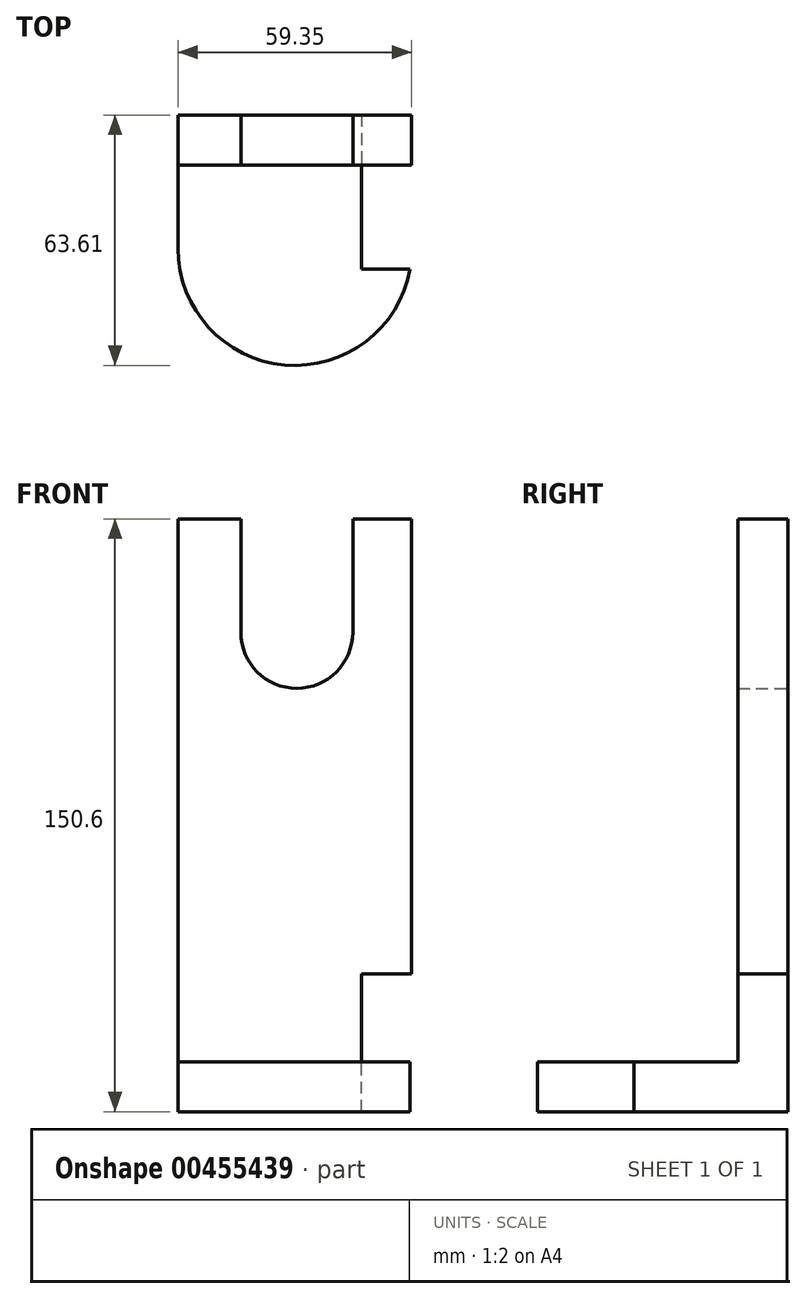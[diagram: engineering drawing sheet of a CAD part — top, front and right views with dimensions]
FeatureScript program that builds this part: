
annotation { "Feature Type Name" : "Feature", "Feature Type Description" : "" }
export const myFeature = defineFeature(function(context is Context, id is Id, definition is map)
    precondition{}
    {
        {
            var Q0;
            Q0=qCreatedBy(makeId("Front.planeOp"),FACE);
            var sketch = newSketch(context, id + "F0", { "sketchPlane" : qUnion([Q0])});
            skLineSegment(sketch, "E0", {"start": v(-52.9, 53.85) * mm, "end": v(-36.97, 53.85) * mm});
            skLineSegment(sketch, "E1", {"start": v(-36.97, 53.85) * mm, "end": v(-36.97, 25.03) * mm});
            skLineSegment(sketch, "E2", {"start": v(-52.9, 53.85) * mm, "end": v(-52.9, -84.05) * mm});
            skLineSegment(sketch, "E3", {"start": v(-52.9, -84.05) * mm, "end": v(6.45, -84.05) * mm});
            skLineSegment(sketch, "E4", {"start": v(6.45, -84.05) * mm, "end": v(6.45, 53.85) * mm});
            skLineSegment(sketch, "E5", {"start": v(6.45, 53.85) * mm, "end": v(-8.53, 53.85) * mm});
            skLineSegment(sketch, "E6", {"start": v(-8.53, 53.85) * mm, "end": v(-8.53, 25.03) * mm});
            skArc(sketch, "E7", {"start": v(-36.97, 25.03) * mm, "mid": v(-22.75, 10.8) * mm, "end": v(-8.53, 25.03) * mm});
            skSolve(sketch);
        }
        {
            var Q0;
            Q0 = qSketchRegion(id + "F0", true);
            extrude(context, id + "F1", {"entities" : qUnion([Q0]), "depth" : 12.7 * mm});
        }
        {
            var Q0;
            Q0=makeQuery(id+"F1.opExtrude","SWEPT_FACE",FACE,{"disambiguationData":[OSD([sQuery(id+"F0.wireOp",EDGE,"E3")])]});
            var sketch = newSketch(context, id + "F2", { "sketchPlane" : qUnion([Q0])});
            skLineSegment(sketch, "E8.bottom", {"start": v(6.45, 0) * mm, "end": v(-52.9, 0) * mm});
            skLineSegment(sketch, "E8.top", {"start": v(6.45, 33.94) * mm, "end": v(-52.9, 33.94) * mm});
            skLineSegment(sketch, "E8.left", {"start": v(6.45, 0) * mm, "end": v(6.45, 33.94) * mm});
            skLineSegment(sketch, "E8.right", {"start": v(-52.9, 0) * mm, "end": v(-52.9, 33.94) * mm});
            skArc(sketch, "E9", {"start": v(-52.9, 33.94) * mm, "mid": v(-23.23, 63.6) * mm, "end": v(6.45, 33.94) * mm});
            skSolve(sketch);
        }
        {
            var Q0;
            Q0 = qSketchRegion(id + "F2", true);
            extrude(context, id + "F3", {"entities" : qUnion([Q0]), "operationType" : NewBodyOperationType.ADD, "depth" : 12.7 * mm});
        }
        {
            var Q0;
            Q0=makeQuery(id+"F3.boolean.opBoolean","MERGE",FACE,{"derivedFrom":[makeQuery(id+"F1.opExtrude","SWEPT_FACE",FACE,{"disambiguationData":[OSD([sQuery(id+"F0.wireOp",EDGE,"E4")])]}),makeQuery(id+"F3.opExtrude","SWEPT_FACE",FACE,{"disambiguationData":[OSD([sQuery(id+"F2.wireOp",EDGE,"E8.left")])]})]});
            var sketch = newSketch(context, id + "F4", { "sketchPlane" : qUnion([Q0])});
            skLineSegment(sketch, "E10.bottom", {"start": v(0, -96.75) * mm, "end": v(-39.16, -96.75) * mm});
            skLineSegment(sketch, "E10.top", {"start": v(0, -61.7) * mm, "end": v(-39.16, -61.7) * mm});
            skLineSegment(sketch, "E10.left", {"start": v(0, -96.75) * mm, "end": v(0, -61.7) * mm});
            skLineSegment(sketch, "E10.right", {"start": v(-39.16, -96.75) * mm, "end": v(-39.16, -61.7) * mm});
            skSolve(sketch);
        }
        {
            var Q0;
            Q0 = qSketchRegion(id + "F4", true);
            extrude(context, id + "F5", {"entities" : qUnion([Q0]), "operationType" : NewBodyOperationType.REMOVE, "oppositeDirection" : true, "depth" : 12.7 * mm});
        }
    });
